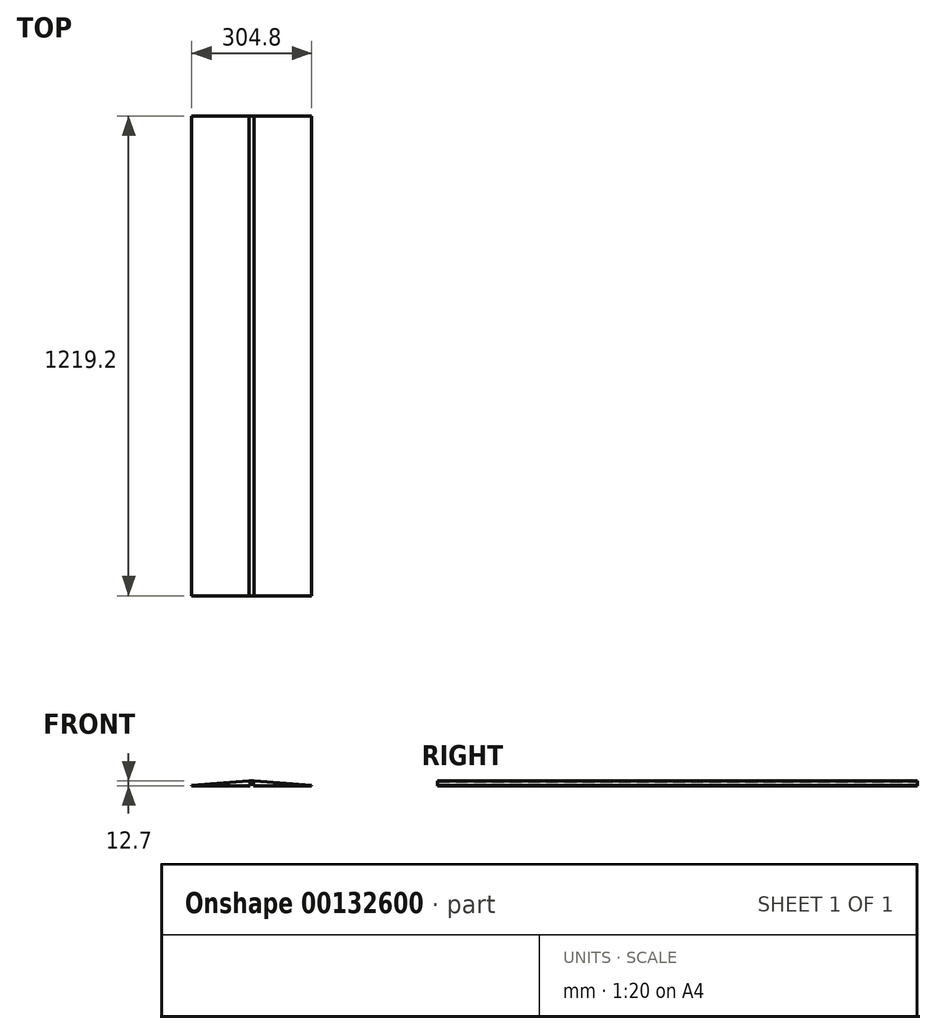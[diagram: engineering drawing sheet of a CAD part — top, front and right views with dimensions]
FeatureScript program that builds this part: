
annotation { "Feature Type Name" : "Feature", "Feature Type Description" : "" }
export const myFeature = defineFeature(function(context is Context, id is Id, definition is map)
    precondition{}
    {
        {
            var Q0;
            Q0=qCreatedBy(makeId("Front.planeOp"),FACE);
            var sketch = newSketch(context, id + "F0", { "sketchPlane" : qUnion([Q0])});
            skLineSegment(sketch, "E0", {"start": v(0, 12.7) * mm, "end": v(-6.35, 12.7) * mm});
            skLineSegment(sketch, "E1", {"start": v(-4.76, 0) * mm, "end": v(-152.4, 0) * mm});
            skLineSegment(sketch, "E2", {"start": v(-152.4, 0) * mm, "end": v(-152.4, 0.76) * mm});
            skLineSegment(sketch, "E3", {"start": v(-152.4, 0.76) * mm, "end": v(-6.35, 12.7) * mm});
            skArc(sketch, "E4", {"start": v(0, 9.53) * mm, "mid": v(-3.37, 8.13) * mm, "end": v(-4.76, 4.76) * mm});
            skLineSegment(sketch, "E5", {"start": v(-4.76, 4.76) * mm, "end": v(-4.76, 0) * mm});
            skLineSegment(sketch, "E6", {"start": v(0, 12.7) * mm, "end": v(0, 9.53) * mm});
            skLineSegment(sketch, "E7.MirrorCS", {"start": v(152.4, 0) * mm, "end": v(152.4, 0.76) * mm});
            skArc(sketch, "E8.MirrorCS", {"start": v(0, 9.53) * mm, "mid": v(3.37, 8.13) * mm, "end": v(4.76, 4.76) * mm});
            skLineSegment(sketch, "E9.MirrorCS", {"start": v(4.76, 4.76) * mm, "end": v(4.76, 0) * mm});
            skLineSegment(sketch, "E10.MirrorCS", {"start": v(0, 12.7) * mm, "end": v(6.35, 12.7) * mm});
            skLineSegment(sketch, "E11.MirrorCS", {"start": v(4.76, 0) * mm, "end": v(152.4, 0) * mm});
            skLineSegment(sketch, "E12.MirrorCS", {"start": v(152.4, 0.76) * mm, "end": v(6.35, 12.7) * mm});
            skSolve(sketch);
        }
        {
            var Q0;
            Q0 = qSketchRegion(id + "F0", true);
            extrude(context, id + "F1", {"entities" : qUnion([Q0]), "endBound" : BoundingType.SYMMETRIC, "depth" : 1219.2 * mm});
        }
    });
